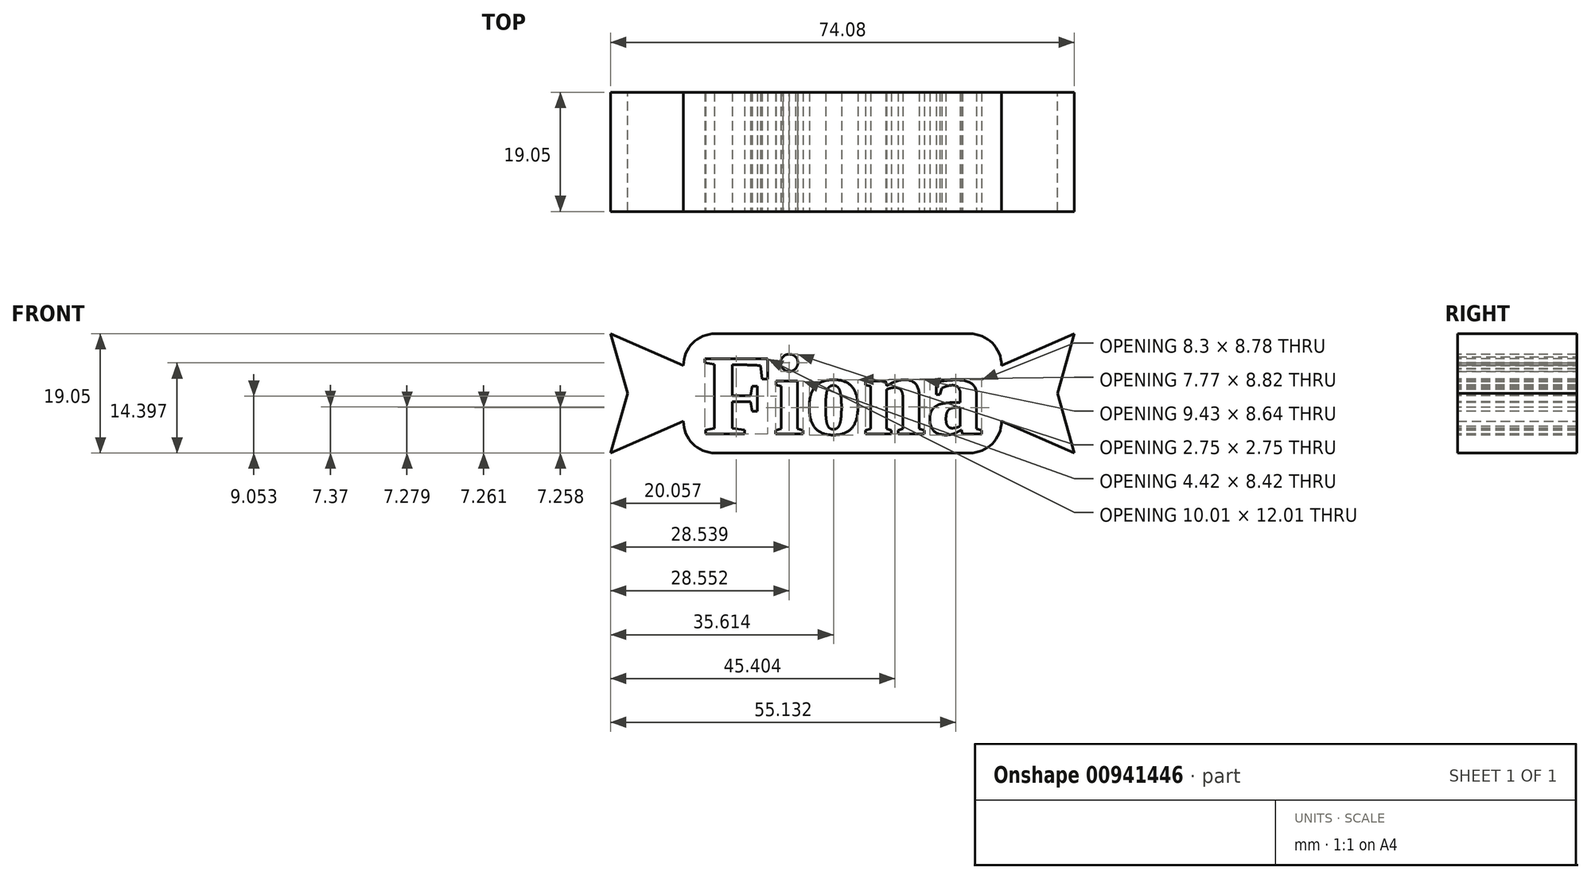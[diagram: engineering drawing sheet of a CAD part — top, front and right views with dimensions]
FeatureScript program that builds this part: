
annotation { "Feature Type Name" : "Feature", "Feature Type Description" : "" }
export const myFeature = defineFeature(function(context is Context, id is Id, definition is map)
    precondition{}
    {
        {
            var Q0;
            Q0=qCreatedBy(makeId("Front.planeOp"),FACE);
            var sketch = newSketch(context, id + "F0", { "sketchPlane" : qUnion([Q0])});
            skLineSegment(sketch, "E0.bottom", {"start": v(-26.57, 7.93) * mm, "end": v(14.07, 7.93) * mm});
            skLineSegment(sketch, "E0.top", {"start": v(-26.57, -11.12) * mm, "end": v(14.07, -11.12) * mm});
            skLineSegment(sketch, "E0.left", {"start": v(-31.65, 2.85) * mm, "end": v(-31.65, -6.04) * mm});
            skLineSegment(sketch, "E0.right", {"start": v(19.15, 2.85) * mm, "end": v(19.15, -6.04) * mm});
            skPoint(sketch, "E1.visualSharp", {"position": v(-31.65, 7.93) * mm});
            skArc(sketch, "E1.filletArc", {"start": v(-26.57, 7.93) * mm, "mid": v(-30.17, 6.44) * mm, "end": v(-31.65, 2.85) * mm});
            skPoint(sketch, "E2.visualSharp", {"position": v(-31.65, -11.12) * mm});
            skArc(sketch, "E2.filletArc", {"start": v(-31.65, -6.04) * mm, "mid": v(-30.17, -9.64) * mm, "end": v(-26.57, -11.12) * mm});
            skPoint(sketch, "E3.visualSharp", {"position": v(19.15, -11.12) * mm});
            skArc(sketch, "E3.filletArc", {"start": v(14.07, -11.12) * mm, "mid": v(17.66, -9.64) * mm, "end": v(19.15, -6.04) * mm});
            skPoint(sketch, "E4.visualSharp", {"position": v(19.15, 7.93) * mm});
            skArc(sketch, "E4.filletArc", {"start": v(19.15, 2.85) * mm, "mid": v(17.66, 6.44) * mm, "end": v(14.07, 7.93) * mm});
            skLineSegment(sketch, "E5", {"start": v(19.15, 2.85) * mm, "end": v(30.79, 7.93) * mm});
            skLineSegment(sketch, "E6", {"start": v(19.15, -6.04) * mm, "end": v(30.79, -11.12) * mm});
            skLineSegment(sketch, "E7", {"start": v(30.79, 7.93) * mm, "end": v(30.79, -11.12) * mm});
            skLineSegment(sketch, "E8", {"start": v(-31.65, 2.85) * mm, "end": v(-43.3, 7.93) * mm});
            skLineSegment(sketch, "E9", {"start": v(-31.65, -6.04) * mm, "end": v(-43.3, -11.12) * mm});
            skLineSegment(sketch, "E10", {"start": v(-43.3, 7.93) * mm, "end": v(-43.3, -11.12) * mm});
            skLineSegment(sketch, "E11", {"start": v(-43.3, 7.93) * mm, "end": v(-40.57, -1.6) * mm});
            skPoint(sketch, "E11.endSnap0", {"position": v(-43.3, -1.6) * mm});
            skLineSegment(sketch, "E12", {"start": v(-40.57, -1.6) * mm, "end": v(-43.3, -11.12) * mm});
            skLineSegment(sketch, "E13", {"start": v(30.79, 7.93) * mm, "end": v(28.07, -1.6) * mm});
            skLineSegment(sketch, "E14", {"start": v(28.07, -1.6) * mm, "end": v(30.79, -11.12) * mm});
            skSolve(sketch);
        }
        {
            var Q0;
            Q0=makeQuery(id+"F0.imprint","IMPRINT",FACE,{"disambiguationData":[TD([[makeQuery(id+"F0.imprint","IMPRINT",EDGE,{"derivedFrom":sQuery(id+"F0.wireOp",EDGE,"E0.bottom")}),-1.0]])]});
            var Q1;
            Q1=makeQuery(id+"F0.imprint","IMPRINT",FACE,{"disambiguationData":[TD([[makeQuery(id+"F0.imprint","IMPRINT",EDGE,{"derivedFrom":sQuery(id+"F0.wireOp",EDGE,"E0.left")}),-1.0]])]});
            var Q2;
            Q2=makeQuery(id+"F0.imprint","IMPRINT",FACE,{"disambiguationData":[TD([[makeQuery(id+"F0.imprint","IMPRINT",EDGE,{"derivedFrom":sQuery(id+"F0.wireOp",EDGE,"E0.right")}),1.0]])]});
            extrude(context, id + "F1", {"entities" : qUnion([Q0, Q1, Q2]), "depth" : 19.05 * mm, "offsetDistance" : 25.4 * mm});
        }
        {
            var Q0;
            Q0=makeQuery(id+"F1.opExtrude","CAP_FACE",FACE,{"disambiguationData":[OSD([sQuery(id+"F0.wireOp",EDGE,"E0.bottom"),sQuery(id+"F0.wireOp",EDGE,"E0.top"),sQuery(id+"F0.wireOp",EDGE,"E1.filletArc"),sQuery(id+"F0.wireOp",EDGE,"E2.filletArc"),sQuery(id+"F0.wireOp",EDGE,"E3.filletArc"),sQuery(id+"F0.wireOp",EDGE,"E4.filletArc"),sQuery(id+"F0.wireOp",EDGE,"E5"),sQuery(id+"F0.wireOp",EDGE,"E6"),sQuery(id+"F0.wireOp",EDGE,"E8"),sQuery(id+"F0.wireOp",EDGE,"E9"),sQuery(id+"F0.wireOp",EDGE,"E11"),sQuery(id+"F0.wireOp",EDGE,"E12"),sQuery(id+"F0.wireOp",EDGE,"E13"),sQuery(id+"F0.wireOp",EDGE,"E14")])],"isStart":false});
            var sketch = newSketch(context, id + "F2", { "sketchPlane" : qUnion([Q0])});
            skText(sketch, "E15", { "text": "Fiona", "fontName": "Tinos-Bold.ttf"});
            const initialGuessF2  = {"E15": [-0.02855, -0.00807, 1, 0, 0.0132]};
            skSetInitialGuess(sketch, initialGuessF2);
            skSolve(sketch);
        }
        {
            var Q0;
            Q0 = qSketchRegion(id + "F2", true);
            extrude(context, id + "F3", {"entities" : qUnion([Q0]), "operationType" : NewBodyOperationType.REMOVE, "oppositeDirection" : true, "depth" : 35.05 * mm, "offsetDistance" : 25.4 * mm});
        }
    });
